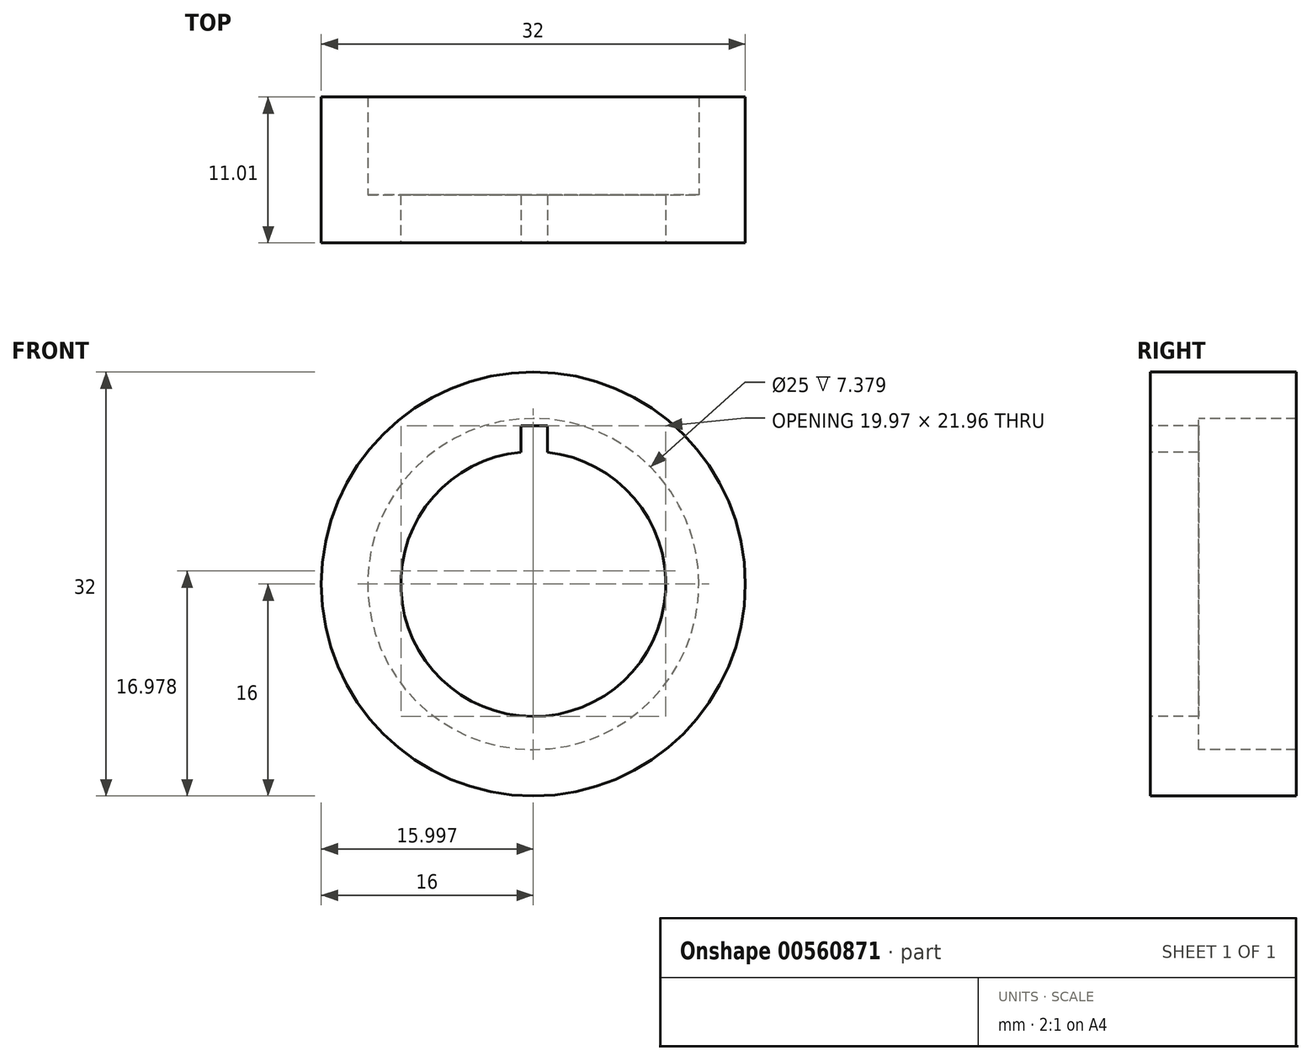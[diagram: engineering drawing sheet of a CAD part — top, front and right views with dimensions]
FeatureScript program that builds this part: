
annotation { "Feature Type Name" : "Feature", "Feature Type Description" : "" }
export const myFeature = defineFeature(function(context is Context, id is Id, definition is map)
    precondition{}
    {
        {
            var Q0;
            Q0=qCreatedBy(makeId("Right.planeOp"),FACE);
            var sketch = newSketch(context, id + "F0", { "sketchPlane" : qUnion([Q0])});
            skLineSegment(sketch, "E0", {"start": v(-47.23, 0) * mm, "end": v(51.02, 0) * mm, "construction": true});
            skLineSegment(sketch, "E1", {"start": v(-17.82, 10) * mm, "end": v(-17.82, 16) * mm});
            skLineSegment(sketch, "E2", {"start": v(-17.82, 16) * mm, "end": v(-6.81, 16) * mm});
            skLineSegment(sketch, "E3", {"start": v(-6.81, 16) * mm, "end": v(-6.81, 12.5) * mm});
            skLineSegment(sketch, "E4", {"start": v(-6.81, 12.5) * mm, "end": v(-14.2, 12.5) * mm});
            skLineSegment(sketch, "E5", {"start": v(-14.2, 12.5) * mm, "end": v(-14.2, 10) * mm});
            skLineSegment(sketch, "E6", {"start": v(-14.2, 10) * mm, "end": v(-17.82, 10) * mm});
            skSolve(sketch);
        }
        {
            var Q0;
            Q0 = qSketchRegion(id + "F0", true);
            var Q1;
            Q1=makeQuery(id+"F0.imprint","IMPRINT",FACE,{"disambiguationData":[TD([[makeQuery(id+"F0.imprint","IMPRINT",EDGE,{"derivedFrom":sQuery(id+"F0.wireOp",EDGE,"E1")}),-1.0]])]});
            var Q2;
            Q2=sQuery(id+"F0.wireOp",EDGE,"E0");
            revolve(context, id + "F1", {"entities" : qUnion([Q0, Q1]), "axis" : qUnion([Q2]), "revolveType" : RevolveType.FULL});
        }
        {
            var Q0;
            Q0=makeQuery(id+"F1.opRevolve","SWEPT_FACE",FACE,{"disambiguationData":[OSD([sQuery(id+"F0.wireOp",EDGE,"E1")])]});
            var sketch = newSketch(context, id + "F2", { "sketchPlane" : qUnion([Q0])});
            skLineSegment(sketch, "E7", {"start": v(-0.94, 9.96) * mm, "end": v(-0.94, 11.96) * mm});
            skLineSegment(sketch, "E8", {"start": v(-0.94, 11.96) * mm, "end": v(1.06, 11.96) * mm});
            skLineSegment(sketch, "E9", {"start": v(1.06, 11.96) * mm, "end": v(1.06, 9.94) * mm});
            skSolve(sketch);
        }
        {
            var Q0;
            Q0 = qSketchRegion(id + "F2", true);
            var Q1;
            {var subQ0=sQuery(id+"F2.wireOp",EDGE,"E7");Q1=makeQuery(id+"F2.imprint","IMPRINT",FACE,{"disambiguationData":[TD([[makeQuery(id+"F2.imprint","IMPRINT",EDGE,{"derivedFrom":subQ0}),-1.0]])]});}
            extrude(context, id + "F3", {"entities" : qUnion([Q0, Q1]), "operationType" : NewBodyOperationType.REMOVE, "oppositeDirection" : true, "depth" : 25 * mm, "offsetDistance" : 25 * mm});
        }
    });
